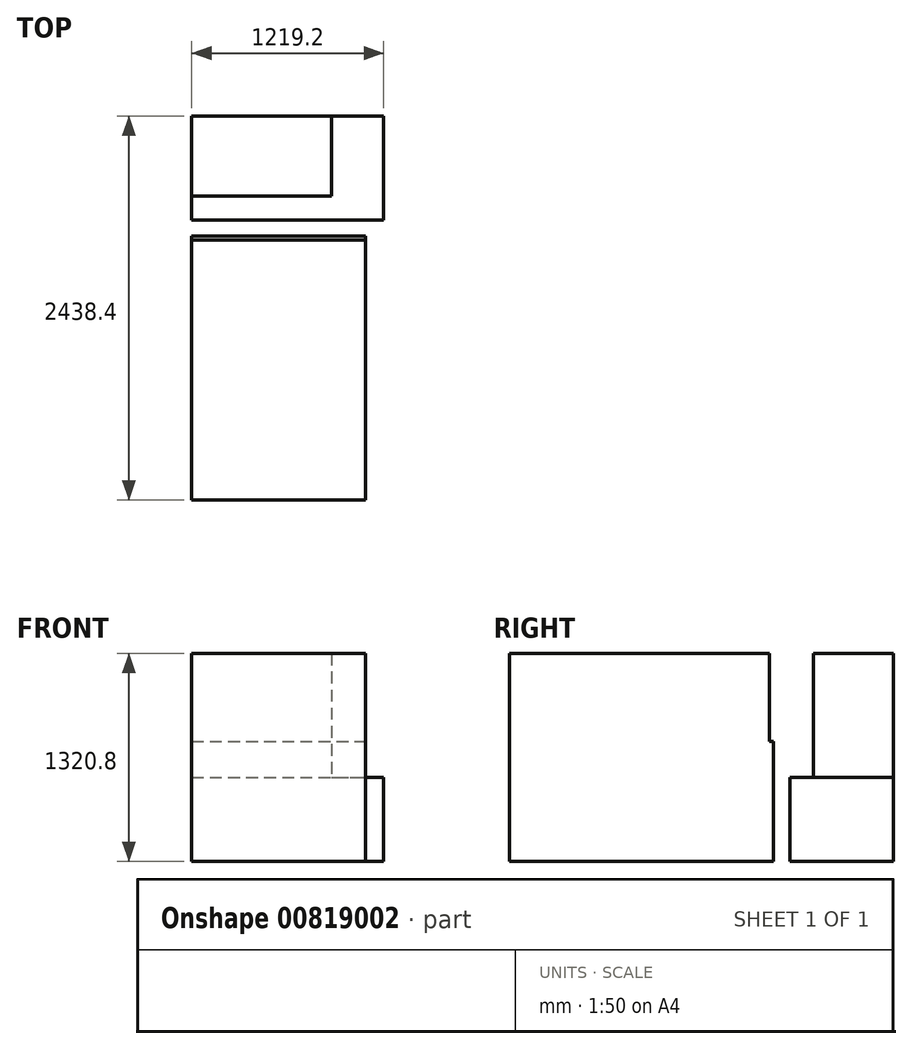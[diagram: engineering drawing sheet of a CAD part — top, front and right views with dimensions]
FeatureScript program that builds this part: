
annotation { "Feature Type Name" : "Feature", "Feature Type Description" : "" }
export const myFeature = defineFeature(function(context is Context, id is Id, definition is map)
    precondition{}
    {
        {
            var Q0;
            Q0=qCreatedBy(makeId("Top.planeOp"),FACE);
            var sketch = newSketch(context, id + "F0", { "sketchPlane" : qUnion([Q0])});
            skLineSegment(sketch, "E0.bottom", {"start": v(0, 0) * mm, "end": v(1422.4, 0) * mm});
            skLineSegment(sketch, "E0.top", {"start": v(0, 2438.4) * mm, "end": v(1422.4, 2438.4) * mm});
            skLineSegment(sketch, "E0.left", {"start": v(0, 0) * mm, "end": v(0, 2438.4) * mm});
            skLineSegment(sketch, "E0.right", {"start": v(1422.4, 0) * mm, "end": v(1422.4, 2438.4) * mm});
            skSolve(sketch);
        }
        {
            var Q0;
            Q0=makeQuery(id+"F0.imprint","IMPRINT",FACE,{"disambiguationData":[TD([[makeQuery(id+"F0.imprint","IMPRINT",EDGE,{"derivedFrom":sQuery(id+"F0.wireOp",EDGE,"E0.bottom")}),1.0]])]});
            var sketch = newSketch(context, id + "F1", { "sketchPlane" : qUnion([Q0])});
            skLineSegment(sketch, "E1.bottom", {"start": v(0, 0) * mm, "end": v(1104.9, 0) * mm});
            skLineSegment(sketch, "E1.top", {"start": v(0, 1676.4) * mm, "end": v(1104.9, 1676.4) * mm});
            skLineSegment(sketch, "E1.left", {"start": v(0, 0) * mm, "end": v(0, 1676.4) * mm});
            skLineSegment(sketch, "E1.right", {"start": v(1104.9, 0) * mm, "end": v(1104.9, 1676.4) * mm});
            skSolve(sketch);
        }
        {
            var Q0;
            Q0=makeQuery(id+"F1.imprint","IMPRINT",FACE,{"disambiguationData":[TD([[makeQuery(id+"F1.imprint","IMPRINT",EDGE,{"derivedFrom":sQuery(id+"F1.wireOp",EDGE,"E1.bottom")}),1.0]])]});
            extrude(context, id + "F2", {"entities" : qUnion([Q0]), "depth" : 762 * mm, "offsetDistance" : 25.4 * mm});
        }
        {
            var Q0;
            Q0=makeQuery(id+"F2.opExtrude","CAP_FACE",FACE,{"disambiguationData":[OSD([sQuery(id+"F1.wireOp",EDGE,"E1.bottom"),sQuery(id+"F1.wireOp",EDGE,"E1.top"),sQuery(id+"F1.wireOp",EDGE,"E1.left"),sQuery(id+"F1.wireOp",EDGE,"E1.right")])],"isStart":false});
            var sketch = newSketch(context, id + "F3", { "sketchPlane" : qUnion([Q0])});
            skLineSegment(sketch, "E2.bottom", {"start": v(0, 0) * mm, "end": v(1117.6, 0) * mm});
            skLineSegment(sketch, "E2.top", {"start": v(0, 1651) * mm, "end": v(1117.6, 1651) * mm});
            skLineSegment(sketch, "E2.left", {"start": v(0, 0) * mm, "end": v(0, 1651) * mm});
            skLineSegment(sketch, "E2.right", {"start": v(1117.6, 0) * mm, "end": v(1117.6, 1651) * mm});
            skSolve(sketch);
        }
        {
            var Q0;
            {var subQ0=sQuery(id+"F3.wireOp",EDGE,"E2.left");Q0=makeQuery(id+"F3.imprint","IMPRINT",FACE,{"disambiguationData":[TD([[makeQuery(id+"F3.imprint","IMPRINT",EDGE,{"derivedFrom":subQ0}),-1.0]])]});}
            extrude(context, id + "F4", {"entities" : qUnion([Q0]), "operationType" : NewBodyOperationType.ADD, "depth" : 558.8 * mm, "offsetDistance" : 25.4 * mm});
        }
        {
            var Q0;
            Q0=makeQuery(id+"F0.imprint","IMPRINT",FACE,{"disambiguationData":[TD([[makeQuery(id+"F0.imprint","IMPRINT",EDGE,{"derivedFrom":sQuery(id+"F0.wireOp",EDGE,"E0.bottom")}),1.0]])]});
            var sketch = newSketch(context, id + "F5", { "sketchPlane" : qUnion([Q0])});
            skLineSegment(sketch, "E3.bottom", {"start": v(0, 2439.54) * mm, "end": v(1219.2, 2439.54) * mm});
            skLineSegment(sketch, "E3.top", {"start": v(0, 1779.14) * mm, "end": v(1219.2, 1779.14) * mm});
            skLineSegment(sketch, "E3.left", {"start": v(0, 2439.54) * mm, "end": v(0, 1779.14) * mm});
            skLineSegment(sketch, "E3.right", {"start": v(1219.2, 2439.54) * mm, "end": v(1219.2, 1779.14) * mm});
            skSolve(sketch);
        }
        {
            var Q0;
            {var subQ0=sQuery(id+"F5.wireOp",EDGE,"E3.top");Q0=makeQuery(id+"F5.imprint","IMPRINT",FACE,{"disambiguationData":[TD([[makeQuery(id+"F5.imprint","IMPRINT",EDGE,{"derivedFrom":subQ0}),1.0]])]});}
            extrude(context, id + "F6", {"entities" : qUnion([Q0]), "depth" : 533.4 * mm, "offsetDistance" : 25.4 * mm});
        }
        {
            var Q0;
            Q0=makeQuery(id+"F6.opExtrude","CAP_FACE",FACE,{"disambiguationData":[OSD([sQuery(id+"F0.wireOp",EDGE,"E0.top"),sQuery(id+"F5.wireOp",EDGE,"E3.top"),sQuery(id+"F5.wireOp",EDGE,"E3.left"),sQuery(id+"F5.wireOp",EDGE,"E3.right")])],"isStart":false});
            var sketch = newSketch(context, id + "F7", { "sketchPlane" : qUnion([Q0])});
            skLineSegment(sketch, "E4.bottom", {"start": v(0, 2438.4) * mm, "end": v(889, 2438.4) * mm});
            skLineSegment(sketch, "E4.top", {"start": v(0, 1930.4) * mm, "end": v(889, 1930.4) * mm});
            skLineSegment(sketch, "E4.left", {"start": v(0, 2438.4) * mm, "end": v(0, 1930.4) * mm});
            skLineSegment(sketch, "E4.right", {"start": v(889, 2438.4) * mm, "end": v(889, 1930.4) * mm});
            skSolve(sketch);
        }
        {
            var Q0;
            Q0=makeQuery(id+"F7.imprint","IMPRINT",FACE,{"disambiguationData":[TD([[makeQuery(id+"F7.imprint","IMPRINT",EDGE,{"derivedFrom":sQuery(id+"F7.wireOp",EDGE,"E4.bottom")}),-1.0]])]});
            extrude(context, id + "F8", {"entities" : qUnion([Q0]), "operationType" : NewBodyOperationType.ADD, "depth" : 787.4 * mm, "offsetDistance" : 25.4 * mm});
        }
    });
